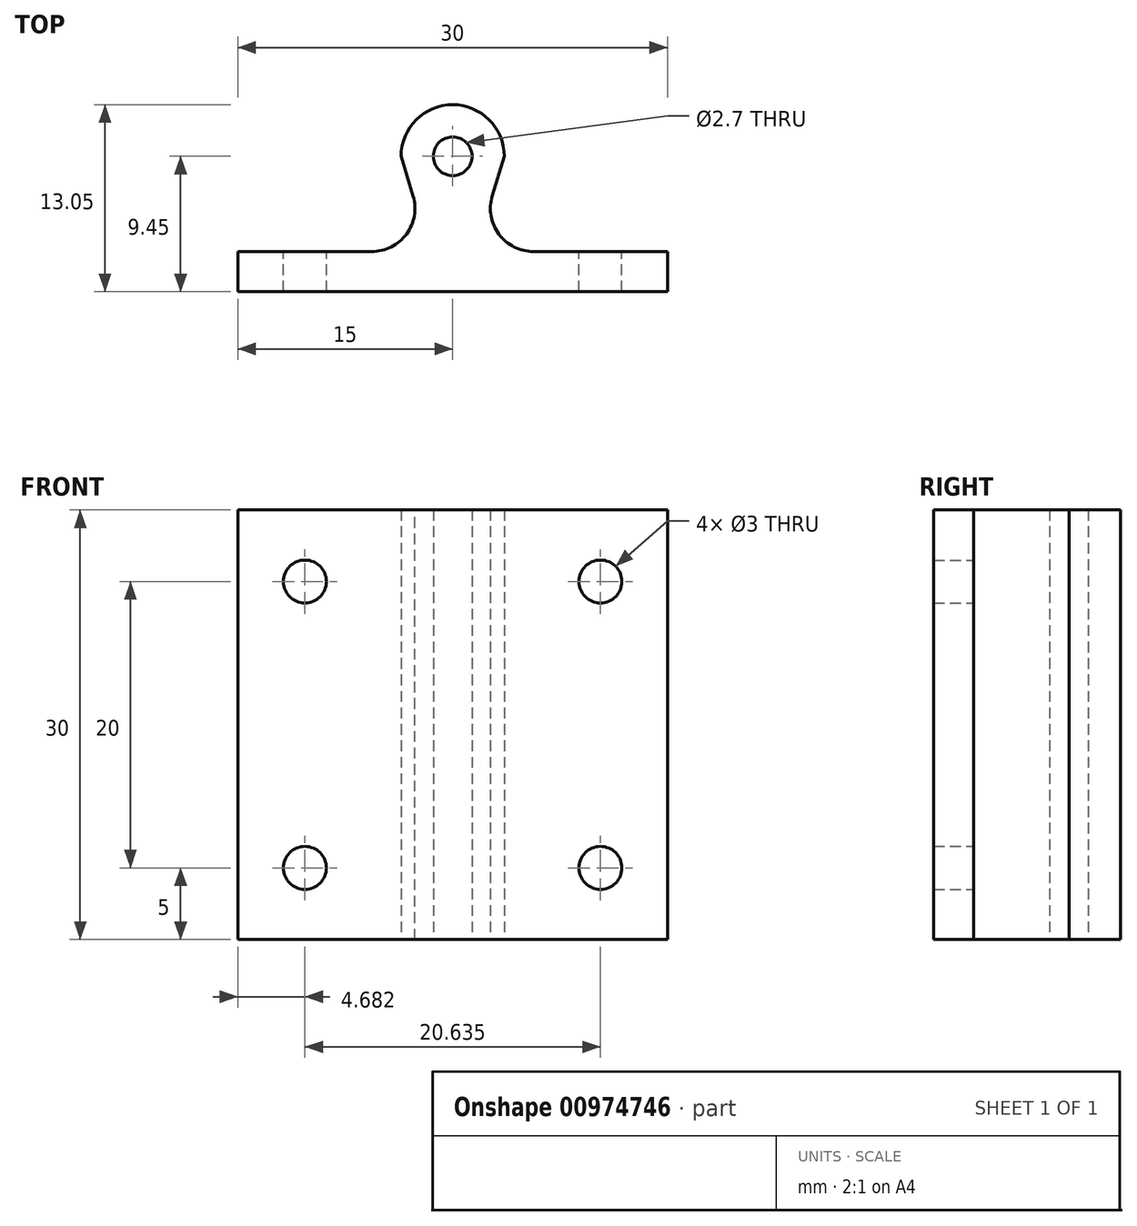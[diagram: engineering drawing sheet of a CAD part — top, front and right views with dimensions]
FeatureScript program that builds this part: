
annotation { "Feature Type Name" : "Feature", "Feature Type Description" : "" }
export const myFeature = defineFeature(function(context is Context, id is Id, definition is map)
    precondition{}
    {
        {
            var Q0;
            Q0=qCreatedBy(makeId("Top.planeOp"),FACE);
            var sketch = newSketch(context, id + "F0", { "sketchPlane" : qUnion([Q0])});
            skLineSegment(sketch, "E0.bottom", {"start": v(15, 0) * mm, "end": v(-15, 0) * mm});
            skLineSegment(sketch, "E0.top", {"start": v(15, 2.8) * mm, "end": v(-15, 2.8) * mm});
            skLineSegment(sketch, "E0.left", {"start": v(15, 0) * mm, "end": v(15, 2.8) * mm});
            skLineSegment(sketch, "E0.right", {"start": v(-15, 0) * mm, "end": v(-15, 2.8) * mm});
            skCircle(sketch, "E1", {"center": v(0, 9.45) * mm, "radius": 1.35 * mm});
            skCircle(sketch, "E2", {"center": v(0, 9.45) * mm, "radius": 3.6 * mm});
            skLineSegment(sketch, "E3", {"start": v(3.6, 9.45) * mm, "end": v(1.6, 2.8) * mm});
            skLineSegment(sketch, "E4", {"start": v(-3.6, 9.45) * mm, "end": v(-1.6, 2.8) * mm});
            skSolve(sketch);
        }
        {
            var Q0;
            Q0=makeQuery(id+"F0.imprint","IMPRINT",FACE,{"disambiguationData":[TD([[makeQuery(id+"F0.imprint","IMPRINT",EDGE,{"derivedFrom":sQuery(id+"F0.wireOp",EDGE,"E1")}),-1.0]])]});
            var Q1;
            {var subQ0=sQuery(id+"F0.wireOp",EDGE,"E3");var subQ1=sQuery(id+"F0.wireOp",EDGE,"E0.top");var subQ2=makeQuery(id+"F0.imprint","INTERSECT",VERTEX,{"derivedFrom":[subQ1,subQ0]});Q1=makeQuery(id+"F0.imprint","IMPRINT",FACE,{"disambiguationData":[TD([[makeQuery(id+"F0.imprint","IMPRINT",EDGE,{"disambiguationData":[TD([[subQ2,-1.0]])],"derivedFrom":subQ1}),-1.0]])]});}
            var Q2;
            Q2=makeQuery(id+"F0.imprint","IMPRINT",FACE,{"disambiguationData":[TD([[makeQuery(id+"F0.imprint","IMPRINT",EDGE,{"derivedFrom":sQuery(id+"F0.wireOp",EDGE,"E0.bottom")}),-1.0]])]});
            extrude(context, id + "F1", {"entities" : qUnion([Q0, Q1, Q2]), "depth" : 30 * mm, "offsetDistance" : 25 * mm});
        }
        {
            var Q0;
            Q0=makeQuery(id+"F1.opExtrude","SWEPT_EDGE",EDGE,{"disambiguationData":[OSD([sQuery(id+"F0.wireOp",EDGE,"E0.top"),sQuery(id+"F0.wireOp",EDGE,"E4")])]});
            var Q1;
            Q1=makeQuery(id+"F1.opExtrude","SWEPT_EDGE",EDGE,{"disambiguationData":[OSD([sQuery(id+"F0.wireOp",EDGE,"E0.top"),sQuery(id+"F0.wireOp",EDGE,"E3")])]});
            fillet(context, id + "F2", {"entities" : qUnion([Q0, Q1]), "radius" : 3 * mm, "tangentPropagation" : true, "allowEdgeOverflow" : false});
        }
        {
            var Q0;
            {var subQ0=sQuery(id+"F0.wireOp",EDGE,"E0.top");Q0=makeQuery(id+"F1.opExtrude","SWEPT_FACE",FACE,{"disambiguationData":[OSD([subQ0]),TDD([makeQuery(id+"F0.imprint","IMPRINT",EDGE,{"disambiguationData":[TD([[makeQuery(id+"F0.imprint","INTERSECT",VERTEX,{"derivedFrom":[subQ0,sQuery(id+"F0.wireOp",EDGE,"E0.left")]}),-1.0]])],"derivedFrom":subQ0})])]});}
            var sketch = newSketch(context, id + "F3", { "sketchPlane" : qUnion([Q0])});
            skCircle(sketch, "E5", {"center": v(-10.32, 25) * mm, "radius": 1.5 * mm});
            skPoint(sketch, "E5.centerSnap0", {"position": v(-10.32, 30) * mm});
            skCircle(sketch, "E6", {"center": v(10.32, 25) * mm, "radius": 1.5 * mm});
            skCircle(sketch, "E7", {"center": v(-10.32, 5) * mm, "radius": 1.5 * mm});
            skCircle(sketch, "E8", {"center": v(10.32, 5) * mm, "radius": 1.5 * mm});
            skSolve(sketch);
        }
        {
            var Q0;
            Q0=makeQuery(id+"F3.imprint","IMPRINT",FACE,{"disambiguationData":[TD([[makeQuery(id+"F3.imprint","IMPRINT",EDGE,{"derivedFrom":sQuery(id+"F3.wireOp",EDGE,"E5")}),1.0]])]});
            var Q1;
            Q1=makeQuery(id+"F3.imprint","IMPRINT",FACE,{"disambiguationData":[TD([[makeQuery(id+"F3.imprint","IMPRINT",EDGE,{"derivedFrom":sQuery(id+"F3.wireOp",EDGE,"E7")}),1.0]])]});
            var Q2;
            Q2=makeQuery(id+"F3.imprint","IMPRINT",FACE,{"disambiguationData":[TD([[makeQuery(id+"F3.imprint","IMPRINT",EDGE,{"derivedFrom":sQuery(id+"F3.wireOp",EDGE,"E8")}),1.0]])]});
            var Q3;
            Q3=makeQuery(id+"F3.imprint","IMPRINT",FACE,{"disambiguationData":[TD([[makeQuery(id+"F3.imprint","IMPRINT",EDGE,{"derivedFrom":sQuery(id+"F3.wireOp",EDGE,"E6")}),1.0]])]});
            extrude(context, id + "F4", {"entities" : qUnion([Q0, Q1, Q2, Q3]), "operationType" : NewBodyOperationType.REMOVE, "oppositeDirection" : true, "depth" : 25 * mm, "offsetDistance" : 25 * mm});
        }
    });
